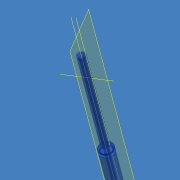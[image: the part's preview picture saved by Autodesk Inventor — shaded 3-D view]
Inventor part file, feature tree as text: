
AUTODESK INVENTOR PART (.ipt)
format: ipt  version: 2013 (Build 170138000, 138)  size: 172,032 bytes
history: native  units: mm
features: other x5, sketch x5, hole x5, projected_geometry x2, plane x1
ambient origin geometry x8: Origin, YZ Plane, XZ Plane, XY Plane, X Axis, Y Axis, Z Axis, Center Point
bodies: Volumenkörper1 (feature_tree)
feature tree (18):
  other  "Drehung2"
  plane  "Arbeitsebene1"
  other  "Arbeitsachse3"
  other  "Arbeitsachse5"
  sketch  "Skizze3"  dims[d21=7.0mm d22=5.925mm]
  other  "Arbeitsachse7"
  hole  "Bohrung1"  [1 undecoded]
  other  "Arbeitspunkt3"
  hole  "Bohrung2"  [1 undecoded]
  hole  "Bohrung3"  [1 undecoded]
  hole  "Bohrung10"  [1 undecoded]
  hole  "Bohrung11"  [1 undecoded]
  sketch  "Skizze1"  dims[d19=14.0mm d20=15.0mm]
  projected_geometry  "Projizierte Kontur1"
  sketch  "Skizze4"  dims[d23=4.5mm d24=3.5mm]
  projected_geometry  "Projizierte Kontur3"
  sketch  "Skizze17"  dims[d26=8.21527mm d27=45.0deg]
  sketch  "Skizze19"  dims[d31=90.0deg d33=2.5mm d34=1.3mm d35=87.48mm d37=1.5mm d38=6.0mm d39=4.0mm d40=2.0mm d41=90.0deg d42=3.5mm d43=0.0mm d44=0.6mm d45=0.1mm d46=10.0mm d47=10.0mm d48=4.0mm d49=6.0mm d50=4.0mm d51=2.0mm d52=90.0deg d53=223.0mm d54=0.0mm d56=1.5mm d57=6.0mm d58=4.0mm d59=2.0mm d60=90.0deg d61=8.0mm d62=0.0mm d64=1.0mm d127=16.0mm d128=8.0mm d129=7.0mm d130=9.0mm d132=90.0deg d135=7.0mm d136=3.5mm d137=3.5mm d138=1.567mm d139=6.0mm d140=4.0mm d141=2.0mm d142=90.0deg d143=6.0mm d144=20.594885mm d145=12.5mm d148=10.0mm d152=189.905mm d153=174.905mm d154=111.2mm d156=81.2mm d157=2.425mm d158=65.48mm d159=5.0mm d160=6.0mm d161=4.0mm d162=2.0mm d163=90.0deg d164=3.0mm d165=0.0mm d166=22.0mm]
note: 5 required parameter values undecoded (feature->parameter linkage not recoverable at this tier; creation-order binding heuristic only, values carry confidence <= 0.55)
